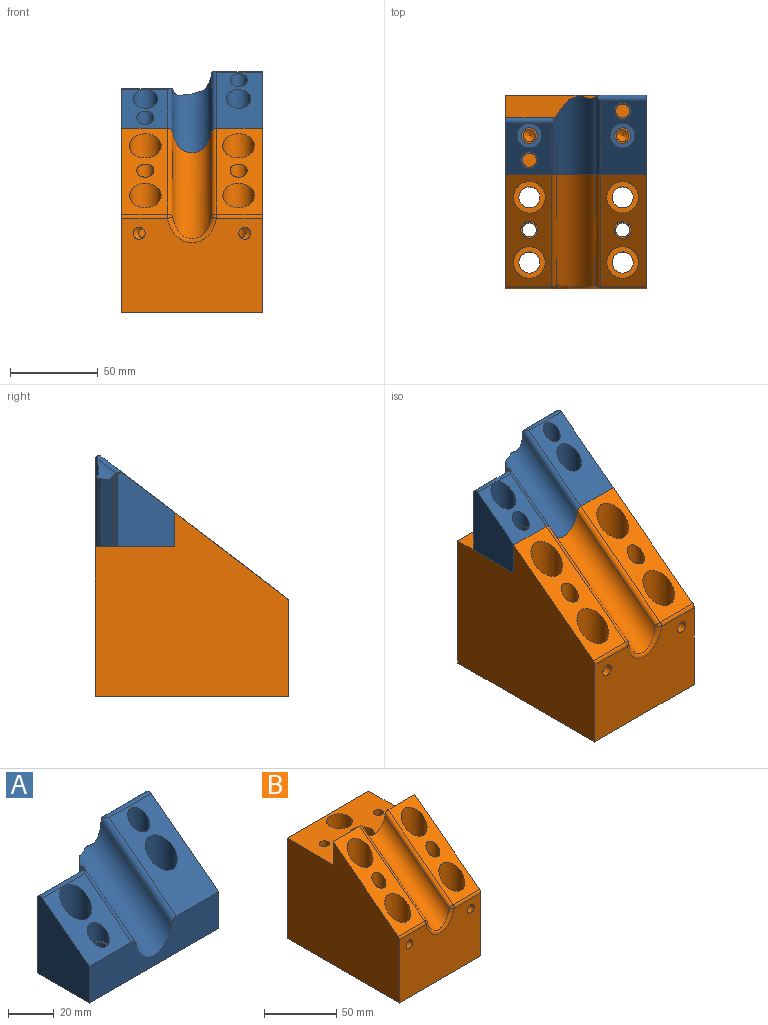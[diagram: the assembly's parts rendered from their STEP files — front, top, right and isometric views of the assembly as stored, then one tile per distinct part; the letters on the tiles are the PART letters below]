
ASSEMBLY  parts=2 mates=1
PART A: 35 faces, bbox 82.2x56.7x54.9 mm
  f0: plane 31.25x28.35mm, normal (0,-0.61,0.79), area 664.8mm2, adj f3,f6,f16,f20,f28,f34
  f1: plane 80x45mm, normal (0,0,-1), area 2933mm2, adj f2,f3,f6,f7,f8,f9,f10,f11
  f2: plane 49.91x26.37mm, normal (0,1,0), area 1316.1mm2, adj f1,f7,f19,f22
  f3: plane 42.15x32.22mm, normal (-1,0,0), area 1024mm2, adj f0,f1,f6,f15,f20
  f4: cylinder r=11.25mm len=54.42mm, axis (0,-0.79,-0.61), area 1575mm2, adj f6,f8,f9,f10,f11,f12,f13,f14
  f5: plane 44.03x34.14mm, normal (0,-0.61,0.79), area 1084.5mm2, adj f6,f7,f17,f22,f25,f31
  f6: plane 80.79x20.39mm, normal (0,-1,0), area 1319.3mm2, adj f0,f1,f3,f4,f5,f7,f16,f17
  f7: plane 51.91x45mm, normal (1,0,0), area 1651.3mm2, adj f1,f2,f5,f6,f22
  f8: cylinder r=7.5mm len=51.63mm, axis (0,0,1), area 391.8mm2, adj f1,f4,f9,f17,f19,f22
  f9: extruded ~40.39x1.54mm, area 64.9mm2, adj f1,f4,f8,f10
  f10: extruded ~40.08x1mm, area 40.8mm2, adj f1,f4,f9,f11
  f11: plane 39.72x4.62mm, normal (-0.32,0.95,0), area 190.6mm2, adj f1,f4,f10,f12
  f12: extruded ~38.88x1.78mm, area 85.7mm2, adj f1,f4,f11,f13
  f13: extruded ~40.46x7.07mm, area 353.5mm2, adj f1,f4,f12,f14
  f14: extruded ~41.72x1.03mm, area 48.6mm2, adj f1,f4,f13,f18
  f15: plane 40.15x27.26mm, normal (0,1,0), area 1094.3mm2, adj f1,f3,f18,f20
  f16: cylinder r=3mm len=34.68mm, axis (0,-0.79,-0.61), area 158.1mm2, adj f0,f4,f6,f20,f21
  f17: cylinder r=3mm len=46.09mm, axis (0,-0.79,-0.61), area 220.3mm2, adj f4,f5,f6,f8,f22
  f18: cylinder r=2mm len=41.92mm, axis (0,0,1), area 99.5mm2, adj f1,f4,f14,f15,f21
  f19: cylinder r=2mm len=51.09mm, axis (0,0,1), area 63.9mm2, adj f1,f2,f8,f22
  f20: cylinder r=2mm len=27.26mm, axis (-1,0,0), area 120.6mm2, adj f0,f3,f15,f16,f21
  f21: bspline ~3.49x3.39mm, area 5mm2, adj f4,f16,f18,f20
  f22: cylinder r=2mm len=28.53mm, axis (-1,0,0), area 121.6mm2, adj f2,f5,f7,f8,f17,f19
  f23: cylinder r=4.5mm len=13.95mm, axis (0,0,1), area 394.4mm2, adj f1,f24
  f24: plane 14x14mm, normal (0,0,1), area 90.3mm2, adj f23,f25
  f25: cylinder r=7mm len=27.79mm, axis (0,0,1), area 987.3mm2, adj f5,f24
  f26: cylinder r=4.5mm len=13.95mm, axis (0,0,1), area 394.4mm2, adj f1,f27
  f27: plane 14x14mm, normal (0,0,1), area 90.3mm2, adj f26,f28
  f28: cylinder r=7mm len=27.79mm, axis (0,0,1), area 987.3mm2, adj f0,f27
  f29: cylinder r=4mm len=18.95mm, axis (0,0,1), area 476.2mm2, adj f1,f30
  f30: plane 9.75x9.75mm, normal (0,0,1), area 24.4mm2, adj f29,f31
  f31: cylinder r=4.88mm len=31.85mm, axis (0,0,1), area 861.7mm2, adj f5,f30
  f32: cylinder r=4mm len=18.95mm, axis (0,0,1), area 476.2mm2, adj f1,f33
  f33: plane 9.75x9.75mm, normal (0,0,1), area 24.4mm2, adj f32,f34
  f34: cylinder r=4.88mm len=10.48mm, axis (0,0,1), area 207.2mm2, adj f0,f33
PART B: 51 faces, bbox 82.9x117x107.5 mm
  f0: cylinder r=9mm len=48.71mm, axis (0,0,1), area 2270.9mm2, adj f5,f29,f47,f50
  f1: cylinder r=9mm len=48.71mm, axis (0,0,1), area 2270.8mm2, adj f4,f31,f45,f49
  f2: cylinder r=4.88mm len=49.68mm, axis (0,0,1), area 1387.8mm2, adj f5,f36,f47,f48
  f3: cylinder r=4.88mm len=49.68mm, axis (0,0,1), area 1387.8mm2, adj f4,f38,f45,f46
  f4: plane 66.71x51.59mm, normal (0,-0.61,0.79), area 1361.4mm2, adj f1,f3,f7,f15,f18,f20,f27
  f5: plane 66.71x51.59mm, normal (0,-0.61,0.79), area 1361.4mm2, adj f0,f2,f6,f12,f13,f20,f34
  f6: plane 110x104.61mm, normal (1,0,0), area 9011.9mm2, adj f5,f8,f9,f10,f13,f19,f20
  f7: plane 110x104.61mm, normal (-1,0,0), area 9011.9mm2, adj f4,f8,f9,f10,f18,f19,f20
  f8: plane 80x53.52mm, normal (0,-1,0), area 3919.4mm2, adj f6,f7,f10,f13,f16,f18,f49,f50
  f9: plane 85x80mm, normal (0,1,0), area 6800mm2, adj f6,f7,f10,f19
  f10: plane 110x80mm, normal (0,0,-1), area 8020.9mm2, adj f6,f7,f8,f9,f25,f28,f30,f32
  f11: cylinder r=11.25mm len=74.47mm, axis (0,-0.79,-0.61), area 2415.6mm2, adj f12,f15,f16,f20
  f12: cylinder r=3mm len=65.24mm, axis (0,-0.79,-0.61), area 321mm2, adj f5,f11,f14,f20
  f13: cylinder r=3mm len=26.1mm, axis (-1,0,0), area 72mm2, adj f5,f6,f8,f14
  f14: sphere r=3mm, area 5.4mm2, adj f12,f13,f16
  f15: cylinder r=3mm len=65.24mm, axis (0,-0.79,-0.61), area 321mm2, adj f4,f11,f17,f20
  f16: bspline ~27.8x14.48mm, area 130.3mm2, adj f8,f11,f14,f17
  f17: sphere r=3mm, area 5.4mm2, adj f15,f16,f18
  f18: cylinder r=3mm len=26.1mm, axis (-1,0,0), area 72mm2, adj f4,f7,f8,f17
  f19: plane 80x45mm, normal (0,0,1), area 3018.4mm2, adj f6,f7,f9,f20,f22,f24,f41,f44
  f20: plane 80.79x20.39mm, normal (0,1,0), area 1319.3mm2, adj f4,f5,f6,f7,f11,f12,f15,f19
  f21: cone r=0mm half-angle=59deg, axis (0,0,1), area 42.4mm2, adj f22
  f22: cylinder r=3.4mm len=23.75mm, axis (0,0,1), area 507.4mm2, adj f19,f21
  f23: cone r=0mm half-angle=59deg, axis (0,0,1), area 42.4mm2, adj f24
  f24: cylinder r=3.4mm len=23.75mm, axis (0,0,1), area 507.4mm2, adj f19,f23
  f25: cylinder r=6mm len=24.61mm, axis (0,0,1), area 927.6mm2, adj f10,f26
  f26: plane 18x18mm, normal (0,0,1), area 141.4mm2, adj f25,f27
  f27: cylinder r=9mm len=76.95mm, axis (0,0,1), area 3949.6mm2, adj f4,f26
  f28: cylinder r=6mm len=24.61mm, axis (0,0,1), area 927.6mm2, adj f10,f29
  f29: plane 18x18mm, normal (0,0,1), area 141.4mm2, adj f0,f28
  f30: cylinder r=6mm len=24.61mm, axis (0,0,1), area 927.6mm2, adj f10,f31
  f31: plane 18x18mm, normal (0,0,1), area 141.4mm2, adj f1,f30
  f32: cylinder r=6mm len=24.61mm, axis (0,0,1), area 927.6mm2, adj f10,f33
  f33: plane 18x18mm, normal (0,0,1), area 141.4mm2, adj f32,f34
  f34: cylinder r=9mm len=76.95mm, axis (0,0,1), area 3949.6mm2, adj f5,f33
  f35: cylinder r=4mm len=34.61mm, axis (0,0,1), area 869.7mm2, adj f10,f36
  f36: plane 9.75x9.75mm, normal (0,0,1), area 24.4mm2, adj f2,f35
  f37: cylinder r=4mm len=34.61mm, axis (0,0,1), area 869.7mm2, adj f10,f38
  f38: plane 9.75x9.75mm, normal (0,0,1), area 24.4mm2, adj f3,f37
  f39: cylinder r=6mm len=25mm, axis (0,0,1), area 942.5mm2, adj f10,f40
  f40: plane 18x18mm, normal (0,0,1), area 141.4mm2, adj f39,f41
  f41: cylinder r=9mm len=60mm, axis (0,0,1), area 3392.9mm2, adj f19,f40
  f42: cylinder r=6mm len=25mm, axis (0,0,1), area 942.5mm2, adj f10,f43
  f43: plane 18x18mm, normal (0,0,1), area 141.4mm2, adj f42,f44
  f44: cylinder r=9mm len=60mm, axis (0,0,1), area 3392.9mm2, adj f19,f43
  f45: cylinder r=3.4mm len=7.97mm, axis (0,-1,0), area 126mm2, adj f1,f3,f46
  f46: cone r=0mm half-angle=59deg, axis (0,-1,0), area 25.7mm2, adj f3,f45
  f47: cylinder r=3.4mm len=7.97mm, axis (0,-1,0), area 126mm2, adj f0,f2,f48
  f48: cone r=0mm half-angle=59deg, axis (0,-1,0), area 25.7mm2, adj f2,f47
  f49: cylinder r=3.4mm len=9.22mm, axis (0,-1,0), area 152.7mm2, adj f1,f8
  f50: cylinder r=3.4mm len=9.22mm, axis (0,-1,0), area 152.7mm2, adj f0,f8
PLACE A t=(0,65,85)mm
PLACE B at identity fixed
MATE fastened A.f1 <-> B.f19  axis (0,0,-1) through (0,65,85)mm
